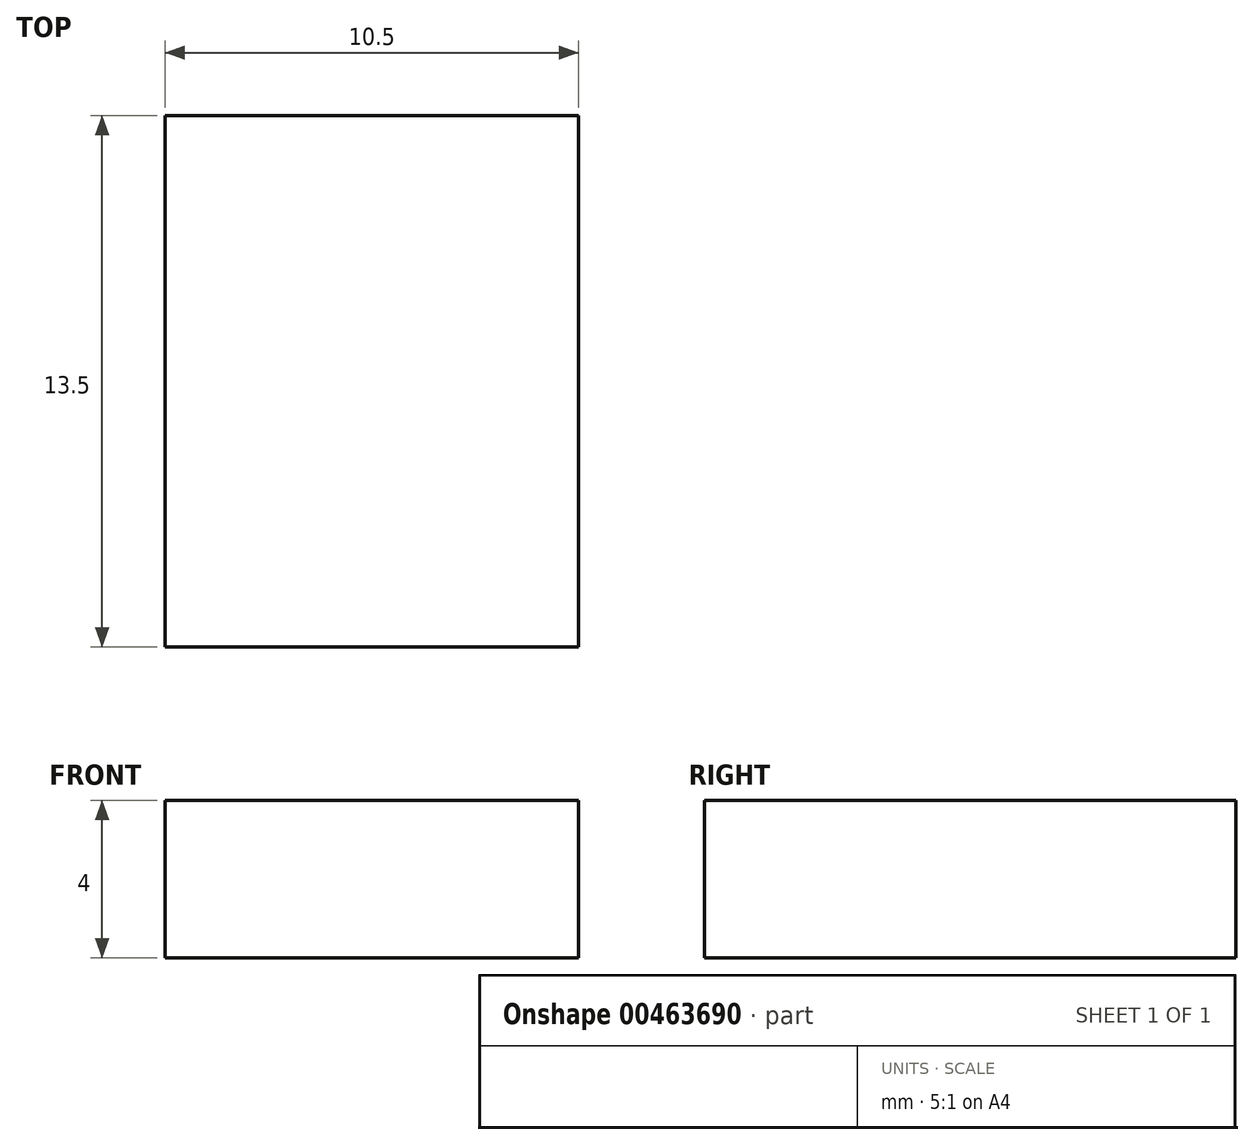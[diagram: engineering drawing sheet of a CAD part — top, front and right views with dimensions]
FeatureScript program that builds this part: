
annotation { "Feature Type Name" : "Feature", "Feature Type Description" : "" }
export const myFeature = defineFeature(function(context is Context, id is Id, definition is map)
    precondition{}
    {
        {
            var Q0;
            Q0=qCreatedBy(makeId("Top.planeOp"),FACE);
            var sketch = newSketch(context, id + "F0", { "sketchPlane" : qUnion([Q0])});
            skLineSegment(sketch, "E0.bottom", {"start": v(-5.25, 6.75) * mm, "end": v(5.25, 6.75) * mm});
            skLineSegment(sketch, "E0.top", {"start": v(-5.25, -6.75) * mm, "end": v(5.25, -6.75) * mm});
            skLineSegment(sketch, "E0.left", {"start": v(-5.25, 6.75) * mm, "end": v(-5.25, -6.75) * mm});
            skLineSegment(sketch, "E0.right", {"start": v(5.25, 6.75) * mm, "end": v(5.25, -6.75) * mm});
            skPoint(sketch, "E0.middle", {"position": v(0, 0) * mm});
            skSolve(sketch);
        }
        {
            var Q0;
            Q0 = qSketchRegion(id + "F0", true);
            extrude(context, id + "F1", {"entities" : qUnion([Q0]), "depth" : 4 * mm});
        }
    });
